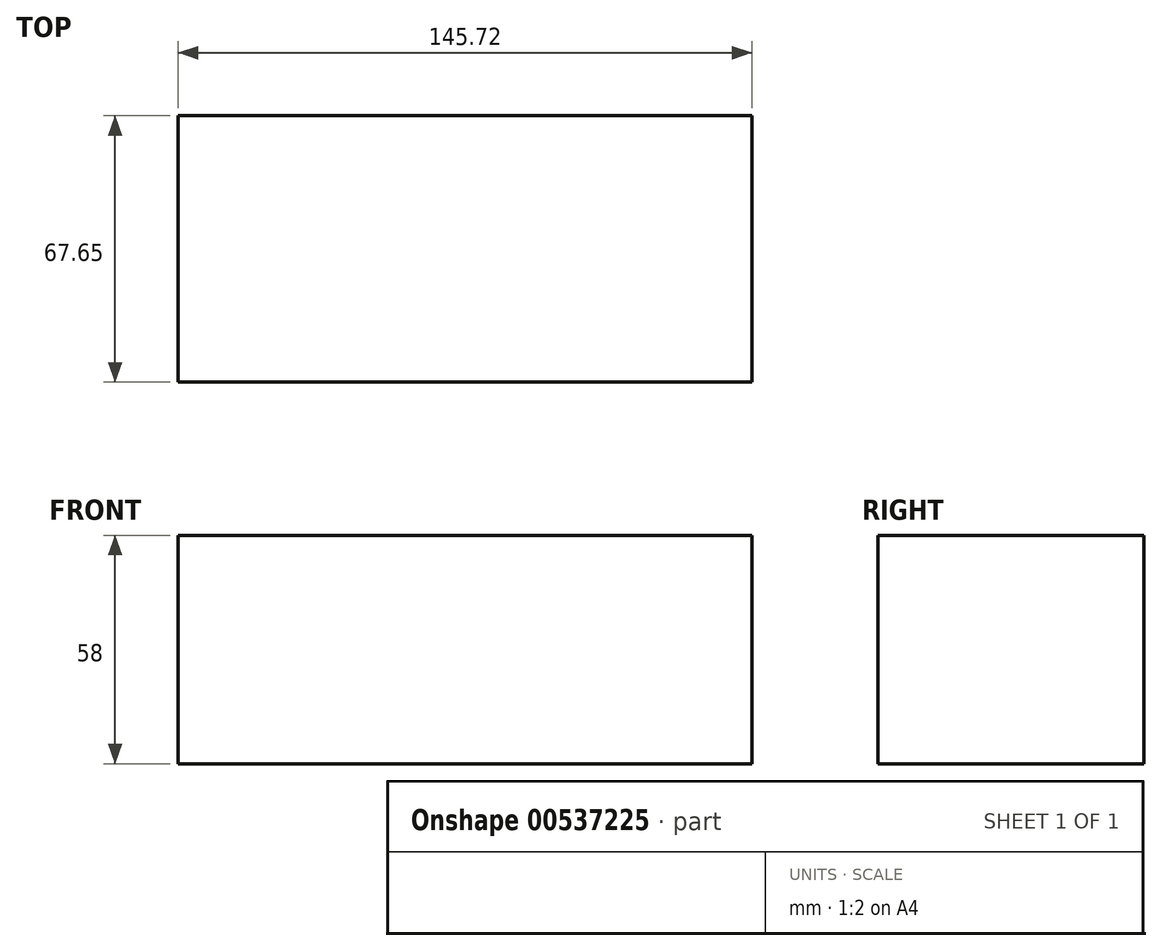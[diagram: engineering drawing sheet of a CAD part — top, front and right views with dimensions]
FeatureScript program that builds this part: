
annotation { "Feature Type Name" : "Feature", "Feature Type Description" : "" }
export const myFeature = defineFeature(function(context is Context, id is Id, definition is map)
    precondition{}
    {
        {
            var Q0;
            Q0=qCreatedBy(makeId("Top.planeOp"),FACE);
            var sketch = newSketch(context, id + "F0", { "sketchPlane" : qUnion([Q0])});
            skLineSegment(sketch, "E0.bottom", {"start": v(-45.66, 18.98) * mm, "end": v(100.06, 18.98) * mm});
            skLineSegment(sketch, "E0.top", {"start": v(-45.66, -48.67) * mm, "end": v(100.06, -48.67) * mm});
            skLineSegment(sketch, "E0.left", {"start": v(-45.66, 18.98) * mm, "end": v(-45.66, -48.67) * mm});
            skLineSegment(sketch, "E0.right", {"start": v(100.06, 18.98) * mm, "end": v(100.06, -48.67) * mm});
            skSolve(sketch);
        }
        {
            var Q0;
            Q0=makeQuery(id+"F0.imprint","IMPRINT",FACE,{"disambiguationData":[TD([[makeQuery(id+"F0.imprint","IMPRINT",EDGE,{"derivedFrom":sQuery(id+"F0.wireOp",EDGE,"E0.bottom")}),-1.0]])]});
            extrude(context, id + "F1", {"entities" : qUnion([Q0]), "oppositeDirection" : true, "depth" : 58 * mm, "offsetDistance" : 25 * mm});
        }
    });
